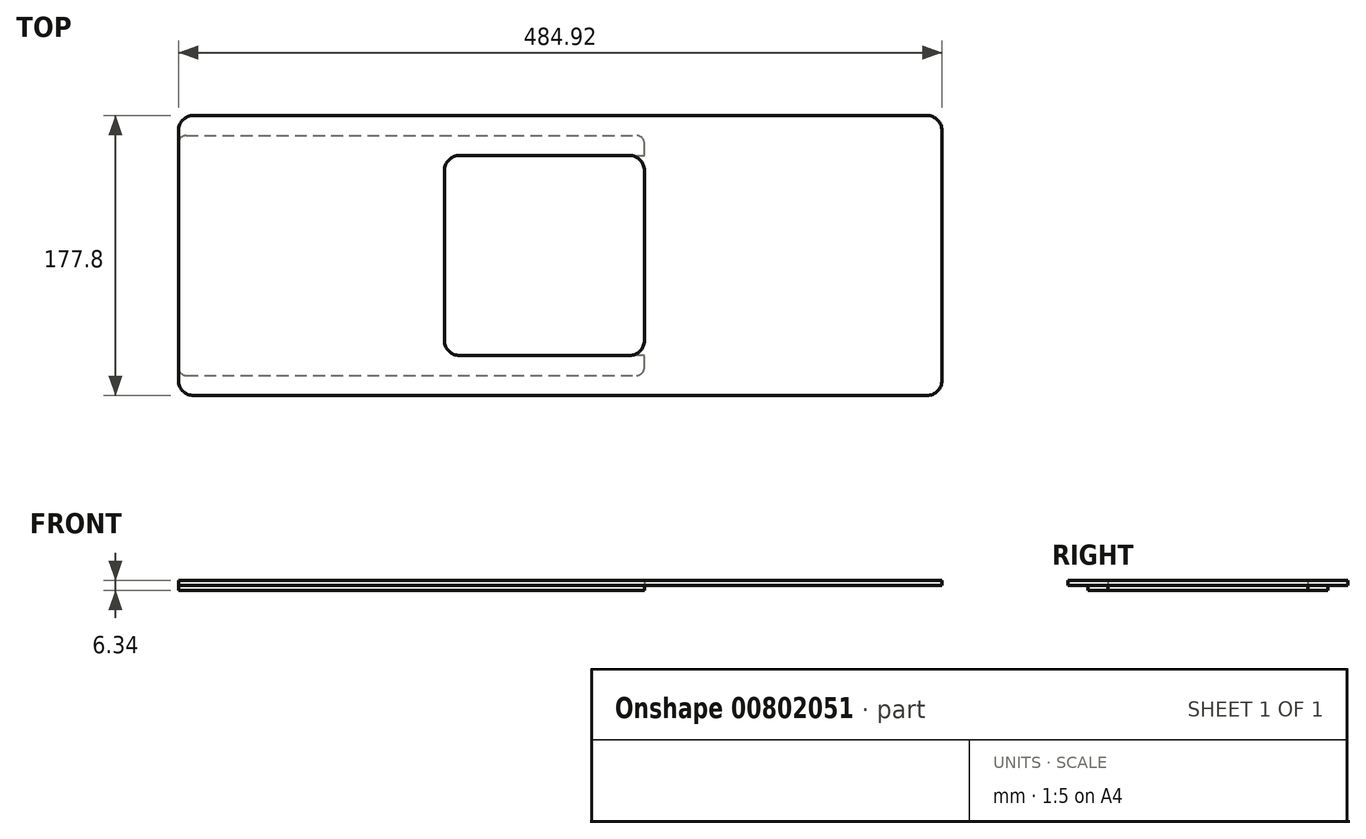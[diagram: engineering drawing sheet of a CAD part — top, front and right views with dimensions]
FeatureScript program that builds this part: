
annotation { "Feature Type Name" : "Feature", "Feature Type Description" : "" }
export const myFeature = defineFeature(function(context is Context, id is Id, definition is map)
    precondition{}
    {
        {
            var Q0;
            Q0=qCreatedBy(makeId("Top.planeOp"),FACE);
            var sketch = newSketch(context, id + "F0", { "sketchPlane" : qUnion([Q0])});
            skLineSegment(sketch, "E0.bottom", {"start": v(-9.53, 0) * mm, "end": v(-117.47, 0) * mm});
            skLineSegment(sketch, "E0.top", {"start": v(-9.53, 127) * mm, "end": v(-117.48, 127) * mm});
            skLineSegment(sketch, "E0.left", {"start": v(0, 9.53) * mm, "end": v(0, 117.47) * mm});
            skLineSegment(sketch, "E0.right", {"start": v(-127, 9.52) * mm, "end": v(-127, 117.47) * mm});
            skPoint(sketch, "E1.visualSharp", {"position": v(-127, 127) * mm});
            skArc(sketch, "E1.filletArc", {"start": v(-117.48, 127) * mm, "mid": v(-124.21, 124.21) * mm, "end": v(-127, 117.47) * mm});
            skPoint(sketch, "E2.visualSharp", {"position": v(0, 127) * mm});
            skArc(sketch, "E2.filletArc", {"start": v(0, 117.47) * mm, "mid": v(-2.79, 124.21) * mm, "end": v(-9.53, 127) * mm});
            skPoint(sketch, "E3.visualSharp", {"position": v(0, 0) * mm});
            skArc(sketch, "E3.filletArc", {"start": v(-9.52, 0) * mm, "mid": v(-2.79, 2.79) * mm, "end": v(0, 9.53) * mm});
            skPoint(sketch, "E4.visualSharp", {"position": v(-127, 0) * mm});
            skArc(sketch, "E4.filletArc", {"start": v(-127, 9.53) * mm, "mid": v(-124.21, 2.79) * mm, "end": v(-117.47, 0) * mm});
            skLineSegment(sketch, "E5.bottom", {"start": v(-286.43, 152.4) * mm, "end": v(179.44, 152.4) * mm});
            skLineSegment(sketch, "E5.top", {"start": v(-286.43, -25.4) * mm, "end": v(179.44, -25.4) * mm});
            skLineSegment(sketch, "E5.left", {"start": v(-295.96, 142.87) * mm, "end": v(-295.96, -15.88) * mm});
            skLineSegment(sketch, "E5.right", {"start": v(188.96, 142.88) * mm, "end": v(188.96, -15.88) * mm});
            skPoint(sketch, "E6.visualSharp", {"position": v(-295.96, 152.4) * mm});
            skArc(sketch, "E6.filletArc", {"start": v(-286.43, 152.4) * mm, "mid": v(-293.17, 149.61) * mm, "end": v(-295.96, 142.87) * mm});
            skPoint(sketch, "E7.visualSharp", {"position": v(188.96, 152.4) * mm});
            skArc(sketch, "E7.filletArc", {"start": v(188.96, 142.88) * mm, "mid": v(186.17, 149.61) * mm, "end": v(179.44, 152.4) * mm});
            skPoint(sketch, "E8.visualSharp", {"position": v(188.96, -25.4) * mm});
            skArc(sketch, "E8.filletArc", {"start": v(179.44, -25.4) * mm, "mid": v(186.17, -22.61) * mm, "end": v(188.96, -15.88) * mm});
            skPoint(sketch, "E9.visualSharp", {"position": v(-295.96, -25.4) * mm});
            skArc(sketch, "E9.filletArc", {"start": v(-295.96, -15.88) * mm, "mid": v(-293.17, -22.61) * mm, "end": v(-286.43, -25.4) * mm});
            skSolve(sketch);
        }
        {
            var Q0;
            Q0=qSketchRegion(id+"F0",true);
            extrude(context, id + "F1", {"entities" : qUnion([Q0]), "depth" : 3.17 * mm});
        }
        {
            var Q0;
            Q0=makeQuery(id+"F1.opExtrude","CAP_FACE",FACE,{"disambiguationData":[OSD([sQuery(id+"F0.wireOp",EDGE,"E0.bottom"),sQuery(id+"F0.wireOp",EDGE,"E0.top"),sQuery(id+"F0.wireOp",EDGE,"E0.left"),sQuery(id+"F0.wireOp",EDGE,"E0.right"),sQuery(id+"F0.wireOp",EDGE,"E1.filletArc"),sQuery(id+"F0.wireOp",EDGE,"E2.filletArc"),sQuery(id+"F0.wireOp",EDGE,"E3.filletArc"),sQuery(id+"F0.wireOp",EDGE,"E4.filletArc"),sQuery(id+"F0.wireOp",EDGE,"E5.bottom"),sQuery(id+"F0.wireOp",EDGE,"E5.top"),sQuery(id+"F0.wireOp",EDGE,"E5.left"),sQuery(id+"F0.wireOp",EDGE,"E5.right"),sQuery(id+"F0.wireOp",EDGE,"E6.filletArc"),sQuery(id+"F0.wireOp",EDGE,"E7.filletArc"),sQuery(id+"F0.wireOp",EDGE,"E8.filletArc"),sQuery(id+"F0.wireOp",EDGE,"E9.filletArc")])],"isStart":true});
            var sketch = newSketch(context, id + "F2", { "sketchPlane" : qUnion([Q0])});
            skLineSegment(sketch, "E10.bottom", {"start": v(-290.96, 12.7) * mm, "end": v(-5, 12.7) * mm});
            skLineSegment(sketch, "E10.top", {"start": v(-290.96, -139.7) * mm, "end": v(-5, -139.7) * mm});
            skLineSegment(sketch, "E10.left", {"start": v(-295.96, 7.7) * mm, "end": v(-295.96, -134.7) * mm});
            skLineSegment(sketch, "E10.right", {"start": v(0, 7.7) * mm, "end": v(0, 0) * mm});
            skLineSegment(sketch, "E11.bottom", {"start": v(-117.47, 0) * mm, "end": v(0, 0) * mm});
            skLineSegment(sketch, "E11.top", {"start": v(-117.48, -127) * mm, "end": v(0, -127) * mm});
            skLineSegment(sketch, "E11.left", {"start": v(-127, -9.53) * mm, "end": v(-127, -117.48) * mm});
            skLineSegment(sketch, "E12.trimOffspring", {"start": v(0, -127) * mm, "end": v(0, -134.7) * mm});
            skPoint(sketch, "E13.visualSharp", {"position": v(-127, 0) * mm});
            skArc(sketch, "E13.filletArc", {"start": v(-117.47, 0) * mm, "mid": v(-124.21, -2.79) * mm, "end": v(-127, -9.53) * mm});
            skPoint(sketch, "E14.visualSharp", {"position": v(-127, -127) * mm});
            skArc(sketch, "E14.filletArc", {"start": v(-127, -117.48) * mm, "mid": v(-124.21, -124.21) * mm, "end": v(-117.48, -127) * mm});
            skPoint(sketch, "E15.visualSharp", {"position": v(0, 12.7) * mm});
            skArc(sketch, "E15.filletArc", {"start": v(0, 7.7) * mm, "mid": v(-1.46, 11.24) * mm, "end": v(-5, 12.7) * mm});
            skPoint(sketch, "E16.visualSharp", {"position": v(-295.96, 12.7) * mm});
            skArc(sketch, "E16.filletArc", {"start": v(-290.96, 12.7) * mm, "mid": v(-294.5, 11.24) * mm, "end": v(-295.96, 7.7) * mm});
            skPoint(sketch, "E17.visualSharp", {"position": v(-295.96, -139.7) * mm});
            skArc(sketch, "E17.filletArc", {"start": v(-295.96, -134.7) * mm, "mid": v(-294.5, -138.24) * mm, "end": v(-290.96, -139.7) * mm});
            skPoint(sketch, "E18.visualSharp", {"position": v(0, -139.7) * mm});
            skArc(sketch, "E18.filletArc", {"start": v(-5, -139.7) * mm, "mid": v(-1.46, -138.24) * mm, "end": v(0, -134.7) * mm});
            skSolve(sketch);
        }
        {
            var Q0;
            Q0=qSketchRegion(id+"F2",true);
            extrude(context, id + "F3", {"entities" : qUnion([Q0]), "operationType" : NewBodyOperationType.ADD, "depth" : 3.17 * mm, "offsetDistance" : 25 * mm});
        }
    });
